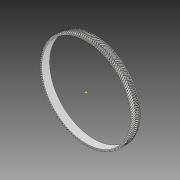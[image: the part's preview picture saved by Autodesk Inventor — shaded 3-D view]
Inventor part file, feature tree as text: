
AUTODESK INVENTOR PART (.ipt)
format: ipt  version: 2020 (Build 240168000, 168)  size: 2,947,072 bytes
history: native  units: in
note: dims shown in document units (in); Inventor stores cm internally (conversion verified against a paired STEP export)
features: other x4, sketch x4, extrude x2, revolve x1, projected_geometry x1
ambient origin geometry x8: Origin, YZ Plane, XZ Plane, XY Plane, X Axis, Y Axis, Z Axis, Center Point
bodies: Solid2 (feature_tree), Solid1 (feature_tree)
feature tree (12):
  other  "Blocks"
  extrude  "Extrusion1"  TaperAngle=0.0deg  [1 undecoded]
  revolve  "Revolution1"  Angle=90.0deg
  extrude  "Extrusion7"  [1 undecoded]
  sketch  "Sketch9"
  sketch  "Sketch1"  dims[d0=0.0in d1=0.0in d23=0.0in]
  other  "Block1"
  other  "Block2"
  sketch  "Sketch7"  dims[d24=0.0394in d25=90.0deg]
  sketch  "Sketch8"  dims[d26=0.0in d27=0.0in]
  projected_geometry  "Projected Loop1"
  other  "Block1:2"
note: 2 required parameter values undecoded (feature->parameter linkage not recoverable at this tier; creation-order binding heuristic only, values carry confidence <= 0.55)
